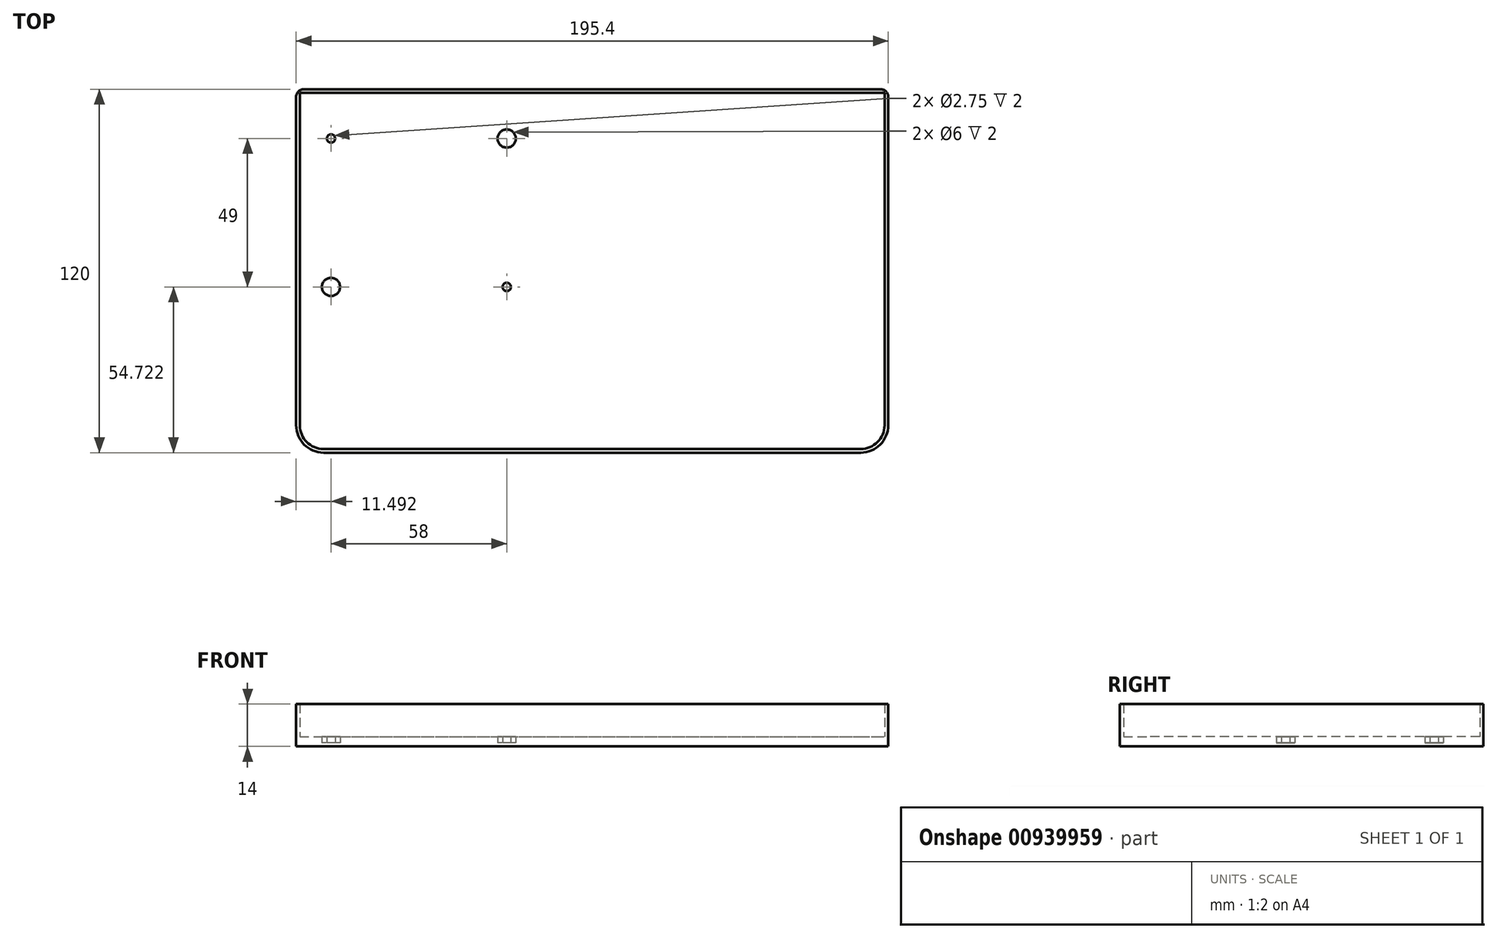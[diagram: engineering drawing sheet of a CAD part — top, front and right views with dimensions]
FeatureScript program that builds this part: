
annotation { "Feature Type Name" : "Feature", "Feature Type Description" : "" }
export const myFeature = defineFeature(function(context is Context, id is Id, definition is map)
    precondition{}
    {
        {
            var Q0;
            Q0=qCreatedBy(makeId("Top.planeOp"),FACE);
            var sketch = newSketch(context, id + "F0", { "sketchPlane" : qUnion([Q0])});
            skLineSegment(sketch, "E0.bottom", {"start": v(-13.54, 27.34) * mm, "end": v(179.46, 27.34) * mm});
            skLineSegment(sketch, "E0.top", {"start": v(-5.68, -90.26) * mm, "end": v(171.6, -90.26) * mm});
            skLineSegment(sketch, "E0.left", {"start": v(-13.54, 27.34) * mm, "end": v(-13.54, -82.4) * mm});
            skLineSegment(sketch, "E0.right", {"start": v(179.46, 27.34) * mm, "end": v(179.46, -82.4) * mm});
            skLineSegment(sketch, "E1.0", {"start": v(-14.74, 28.54) * mm, "end": v(180.66, 28.54) * mm});
            skLineSegment(sketch, "E1.1", {"start": v(-14.74, 28.54) * mm, "end": v(-14.74, -82.4) * mm});
            skLineSegment(sketch, "E1.2", {"start": v(-5.68, -91.46) * mm, "end": v(171.6, -91.46) * mm});
            skLineSegment(sketch, "E1.3", {"start": v(180.66, 28.54) * mm, "end": v(180.66, -82.4) * mm});
            skPoint(sketch, "E2.visualSharp", {"position": v(-13.54, -90.26) * mm});
            skArc(sketch, "E2.filletArc", {"start": v(-13.54, -82.4) * mm, "mid": v(-11.23, -87.95) * mm, "end": v(-5.68, -90.26) * mm});
            skPoint(sketch, "E3.visualSharp", {"position": v(179.46, -90.26) * mm});
            skArc(sketch, "E3.filletArc", {"start": v(171.6, -90.26) * mm, "mid": v(177.16, -87.95) * mm, "end": v(179.46, -82.4) * mm});
            skPoint(sketch, "E4.visualSharp", {"position": v(180.66, -91.46) * mm});
            skArc(sketch, "E4.filletArc", {"start": v(171.6, -91.46) * mm, "mid": v(178.01, -88.8) * mm, "end": v(180.66, -82.4) * mm});
            skPoint(sketch, "E5.visualSharp", {"position": v(-14.74, -91.46) * mm});
            skArc(sketch, "E5.filletArc", {"start": v(-14.74, -82.4) * mm, "mid": v(-12.08, -88.8) * mm, "end": v(-5.68, -91.46) * mm});
            skSolve(sketch);
        }
        {
            var Q0;
            Q0=makeQuery(id+"F0.imprint","IMPRINT",FACE,{"disambiguationData":[TD([[makeQuery(id+"F0.imprint","IMPRINT",EDGE,{"derivedFrom":sQuery(id+"F0.wireOp",EDGE,"E0.bottom")}),-1.0]])]});
            extrude(context, id + "F1", {"entities" : qUnion([Q0]), "depth" : 1.2 * mm, "offsetDistance" : 25 * mm});
        }
        {
            var Q0;
            Q0=makeQuery(id+"F0.imprint","IMPRINT",FACE,{"disambiguationData":[TD([[makeQuery(id+"F0.imprint","IMPRINT",EDGE,{"derivedFrom":sQuery(id+"F0.wireOp",EDGE,"E0.bottom")}),1.0]])]});
            extrude(context, id + "F2", {"entities" : qUnion([Q0]), "operationType" : NewBodyOperationType.ADD, "depth" : 14 * mm, "offsetDistance" : 25 * mm});
        }
        {
            var Q0;
            Q0=makeQuery(id+"F2.opExtrude","SWEPT_EDGE",EDGE,{"disambiguationData":[OSD([sQuery(id+"F0.wireOp",EDGE,"E1.0"),sQuery(id+"F0.wireOp",EDGE,"E1.1")])]});
            var Q1;
            Q1=makeQuery(id+"F2.opExtrude","SWEPT_EDGE",EDGE,{"disambiguationData":[OSD([sQuery(id+"F0.wireOp",EDGE,"E1.0"),sQuery(id+"F0.wireOp",EDGE,"E1.3")])]});
            fillet(context, id + "F3", {"entities" : qUnion([Q0, Q1]), "radius" : 2.5 * mm, "tangentPropagation" : true, "allowEdgeOverflow" : false});
        }
        {
            var Q0;
            Q0=makeQuery(id+"F1.opExtrude","CAP_FACE",FACE,{"disambiguationData":[OSD([sQuery(id+"F0.wireOp",EDGE,"E0.bottom"),sQuery(id+"F0.wireOp",EDGE,"E0.top"),sQuery(id+"F0.wireOp",EDGE,"E0.left"),sQuery(id+"F0.wireOp",EDGE,"E0.right"),sQuery(id+"F0.wireOp",EDGE,"E2.filletArc"),sQuery(id+"F0.wireOp",EDGE,"E3.filletArc")])],"isStart":false});
            var sketch = newSketch(context, id + "F4", { "sketchPlane" : qUnion([Q0])});
            skCircle(sketch, "E6", {"center": v(-3.25, 12.26) * mm, "radius": 1.38 * mm});
            skCircle(sketch, "E7.0", {"center": v(-3.25, 12.26) * mm, "radius": 3 * mm});
            skLineSegment(sketch, "E8", {"start": v(-3.25, 12.26) * mm, "end": v(54.75, 12.26) * mm, "construction": true});
            skLineSegment(sketch, "E9", {"start": v(54.75, 12.26) * mm, "end": v(54.75, -36.74) * mm, "construction": true});
            skLineSegment(sketch, "E10", {"start": v(54.75, -36.74) * mm, "end": v(-3.25, -36.74) * mm, "construction": true});
            skLineSegment(sketch, "E11", {"start": v(-3.25, -36.74) * mm, "end": v(-3.25, 12.26) * mm, "construction": true});
            skLineSegment(sketch, "E12", {"start": v(25.75, 12.26) * mm, "end": v(25.75, -36.74) * mm, "construction": true});
            skLineSegment(sketch, "E13", {"start": v(-3.25, -12.24) * mm, "end": v(54.75, -12.24) * mm, "construction": true});
            skCircle(sketch, "E14.MirrorC", {"center": v(54.75, 12.26) * mm, "radius": 3 * mm});
            skCircle(sketch, "E15.MirrorC", {"center": v(54.75, 12.26) * mm, "radius": 1.38 * mm});
            skCircle(sketch, "E16.MirrorC", {"center": v(54.75, -36.74) * mm, "radius": 3 * mm});
            skCircle(sketch, "E17.MirrorC", {"center": v(54.75, -36.74) * mm, "radius": 1.38 * mm});
            skCircle(sketch, "E18.MirrorC", {"center": v(-3.25, -36.74) * mm, "radius": 3 * mm});
            skCircle(sketch, "E19.MirrorC", {"center": v(-3.25, -36.74) * mm, "radius": 1.38 * mm});
            skSolve(sketch);
        }
        {
            var Q0;
            Q0=makeQuery(id+"F4.imprint","IMPRINT",FACE,{"disambiguationData":[TD([[makeQuery(id+"F4.imprint","IMPRINT",EDGE,{"derivedFrom":sQuery(id+"F4.wireOp",EDGE,"E18.MirrorC")}),-1.0]])]});
            var Q1;
            Q1=makeQuery(id+"F4.imprint","IMPRINT",FACE,{"disambiguationData":[TD([[makeQuery(id+"F4.imprint","IMPRINT",EDGE,{"derivedFrom":sQuery(id+"F4.wireOp",EDGE,"E16.MirrorC")}),1.0]])]});
            var Q2;
            Q2=makeQuery(id+"F4.imprint","IMPRINT",FACE,{"disambiguationData":[TD([[makeQuery(id+"F4.imprint","IMPRINT",EDGE,{"derivedFrom":sQuery(id+"F4.wireOp",EDGE,"E14.MirrorC")}),-1.0]])]});
            var Q3;
            Q3=makeQuery(id+"F4.imprint","IMPRINT",FACE,{"disambiguationData":[TD([[makeQuery(id+"F4.imprint","IMPRINT",EDGE,{"derivedFrom":sQuery(id+"F4.wireOp",EDGE,"E6")}),-1.0]])]});
            extrude(context, id + "F5", {"entities" : qUnion([Q0, Q1, Q2, Q3]), "operationType" : NewBodyOperationType.ADD, "depth" : 2 * mm, "offsetDistance" : 25 * mm});
        }
    });
